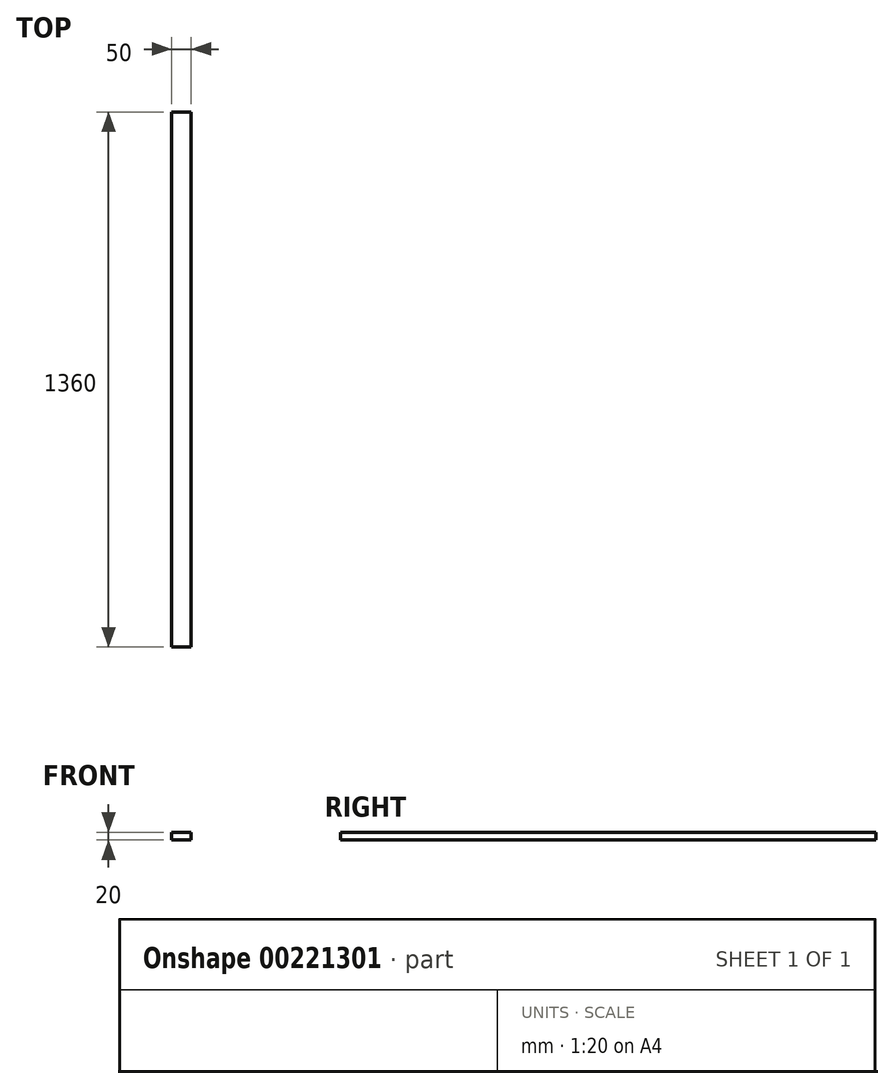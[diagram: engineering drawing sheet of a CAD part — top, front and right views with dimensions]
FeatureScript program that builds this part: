
annotation { "Feature Type Name" : "Feature", "Feature Type Description" : "" }
export const myFeature = defineFeature(function(context is Context, id is Id, definition is map)
    precondition{}
    {
        {
            var Q0;
            Q0=qCreatedBy(makeId("Front.planeOp"),FACE);
            var sketch = newSketch(context, id + "F0", { "sketchPlane" : qUnion([Q0])});
            skLineSegment(sketch, "E0.bottom", {"start": v(-21.52, 12.77) * mm, "end": v(28.48, 12.77) * mm});
            skLineSegment(sketch, "E0.top", {"start": v(-21.52, -7.23) * mm, "end": v(28.48, -7.23) * mm});
            skLineSegment(sketch, "E0.left", {"start": v(-21.52, 12.77) * mm, "end": v(-21.52, -7.23) * mm});
            skLineSegment(sketch, "E0.right", {"start": v(28.48, 12.77) * mm, "end": v(28.48, -7.23) * mm});
            skSolve(sketch);
        }
        {
            var Q0;
            Q0=makeQuery(id+"F0.imprint","IMPRINT",FACE,{"disambiguationData":[TD([[makeQuery(id+"F0.imprint","IMPRINT",EDGE,{"derivedFrom":sQuery(id+"F0.wireOp",EDGE,"E0.bottom")}),-1.0]])]});
            extrude(context, id + "F1", {"entities" : qUnion([Q0]), "oppositeDirection" : true, "depth" : 1360 * mm});
        }
    });
